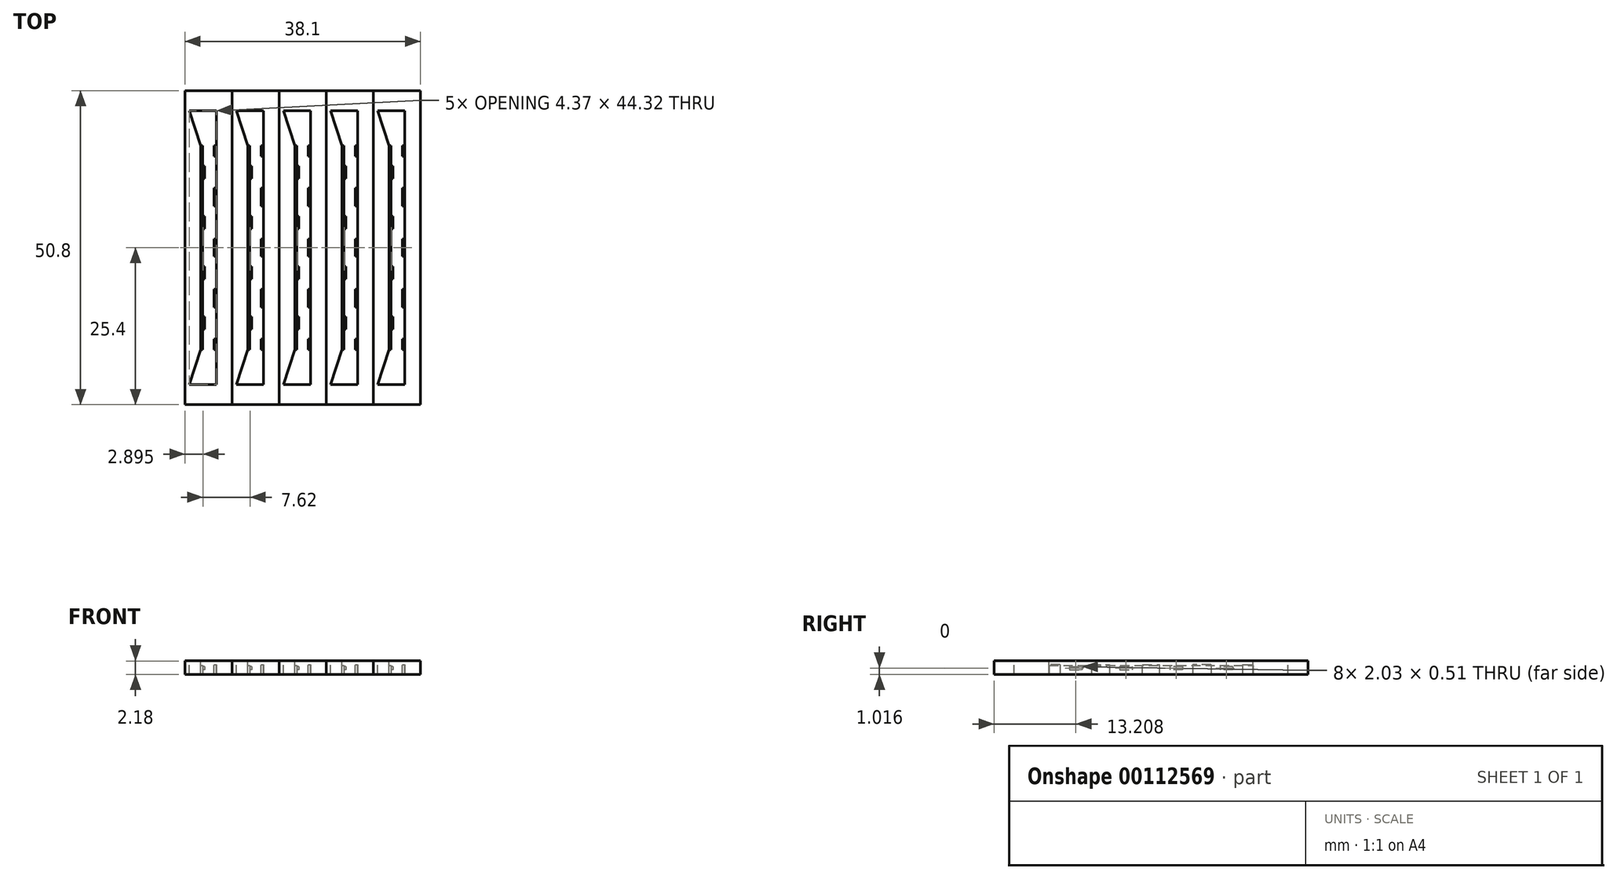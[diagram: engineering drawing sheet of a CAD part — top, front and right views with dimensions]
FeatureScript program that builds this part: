
annotation { "Feature Type Name" : "Feature", "Feature Type Description" : "" }
export const myFeature = defineFeature(function(context is Context, id is Id, definition is map)
    precondition{}
    {
        {
            var Q0;
            Q0=qCreatedBy(makeId("Top.planeOp"),FACE);
            var sketch = newSketch(context, id + "F0", { "sketchPlane" : qUnion([Q0])});
            skLineSegment(sketch, "E0.bottom", {"start": v(3.81, -25.4) * mm, "end": v(-3.81, -25.4) * mm});
            skLineSegment(sketch, "E0.top", {"start": v(3.81, 25.4) * mm, "end": v(-3.81, 25.4) * mm});
            skLineSegment(sketch, "E0.left", {"start": v(3.8, -25.4) * mm, "end": v(3.81, 25.4) * mm});
            skLineSegment(sketch, "E0.right", {"start": v(-3.81, -25.4) * mm, "end": v(-3.81, 25.4) * mm});
            skPoint(sketch, "E0.middle", {"position": v(0, 0) * mm});
            skSolve(sketch);
        }
        {
            var Q0;
            Q0=makeQuery(id+"F0.imprint","IMPRINT",FACE,{"disambiguationData":[TD([[makeQuery(id+"F0.imprint","IMPRINT",EDGE,{"derivedFrom":sQuery(id+"F0.wireOp",EDGE,"E0.bottom")}),-1.0]])]});
            extrude(context, id + "F1", {"entities" : qUnion([Q0]), "depth" : 2.18 * mm});
        }
        {
            var Q0;
            Q0=qCreatedBy(makeId("Front.planeOp"),FACE);
            var sketch = newSketch(context, id + "F2", { "sketchPlane" : qUnion([Q0])});
            skLineSegment(sketch, "E1.bottom", {"start": v(1.27, 0) * mm, "end": v(-0.97, 0) * mm});
            skLineSegment(sketch, "E1.top", {"start": v(1.27, 2.18) * mm, "end": v(-1.27, 2.18) * mm});
            skLineSegment(sketch, "E1.left", {"start": v(1.27, 0) * mm, "end": v(1.27, 2.18) * mm});
            skLineSegment(sketch, "E1.right", {"start": v(-1.27, 1.47) * mm, "end": v(-1.27, 2.18) * mm});
            skPoint(sketch, "E1.middle", {"position": v(0, 1.1) * mm});
            skLineSegment(sketch, "E2", {"start": v(-1.27, 1.47) * mm, "end": v(-0.97, 1.47) * mm});
            skLineSegment(sketch, "E3", {"start": v(-0.97, 1.47) * mm, "end": v(-0.97, 0) * mm});
            skPoint(sketch, "E4.orphan", {"position": v(-1.27, 0) * mm});
            skSolve(sketch);
        }
        {
            var Q0;
            Q0=qSketchRegion(id+"F2",true);
            extrude(context, id + "F3", {"entities" : qUnion([Q0]), "operationType" : NewBodyOperationType.REMOVE, "endBound" : BoundingType.SYMMETRIC, "depth" : 33.02 * mm});
        }
        {
            var Q0;
            Q0=makeQuery(id+"F3.boolean.opBoolean","COPY",FACE,{"derivedFrom":makeQuery(id+"F3.opExtrude","SWEPT_FACE",FACE,{"disambiguationData":[OSD([sQuery(id+"F2.wireOp",EDGE,"E1.left")])]})});
            var sketch = newSketch(context, id + "F4", { "sketchPlane" : qUnion([Q0])});
            skLineSegment(sketch, "E5.bottom", {"start": v(1.4, 0) * mm, "end": v(-1.4, 0) * mm});
            skLineSegment(sketch, "E5.top", {"start": v(1.4, 1.57) * mm, "end": v(-1.4, 1.57) * mm});
            skLineSegment(sketch, "E5.left", {"start": v(1.4, 0) * mm, "end": v(1.4, 1.57) * mm});
            skLineSegment(sketch, "E5.right", {"start": v(-1.4, 0) * mm, "end": v(-1.4, 1.57) * mm});
            skPoint(sketch, "E5.middle", {"position": v(0, 0.79) * mm});
            skLineSegment(sketch, "E6", {"start": v(0, 5.78) * mm, "end": v(0, -5.42) * mm, "construction": true});
            skLineSegment(sketch, "E7", {"start": v(-25.4, 1.57) * mm, "end": v(25.4, 1.57) * mm, "construction": true});
            skLineSegment(sketch, "E8.bottom", {"start": v(-9.68, 1.57) * mm, "end": v(-6.73, 1.57) * mm});
            skLineSegment(sketch, "E8.top", {"start": v(-9.68, 0) * mm, "end": v(-6.73, 0) * mm});
            skLineSegment(sketch, "E8.left", {"start": v(-9.68, 1.57) * mm, "end": v(-9.68, 0) * mm});
            skLineSegment(sketch, "E8.right", {"start": v(-6.73, 1.57) * mm, "end": v(-6.73, 0) * mm});
            skLineSegment(sketch, "E9.MirrorCS", {"start": v(9.68, 1.57) * mm, "end": v(9.68, 0) * mm});
            skLineSegment(sketch, "E10.MirrorCS", {"start": v(25.4, 1.57) * mm, "end": v(-25.4, 1.57) * mm, "construction": true});
            skLineSegment(sketch, "E11.MirrorCS", {"start": v(6.73, 1.57) * mm, "end": v(6.73, 0) * mm});
            skLineSegment(sketch, "E12.MirrorCS", {"start": v(9.68, 0) * mm, "end": v(6.73, 0) * mm});
            skLineSegment(sketch, "E13.MirrorCS", {"start": v(9.68, 1.57) * mm, "end": v(6.73, 1.57) * mm});
            skLineSegment(sketch, "E14.bottom", {"start": v(-14.78, 1.57) * mm, "end": v(-16.51, 1.57) * mm});
            skLineSegment(sketch, "E14.top", {"start": v(-14.78, 0) * mm, "end": v(-16.51, 0) * mm});
            skLineSegment(sketch, "E14.left", {"start": v(-14.78, 1.57) * mm, "end": v(-14.78, 0) * mm});
            skLineSegment(sketch, "E14.right", {"start": v(-16.51, 1.57) * mm, "end": v(-16.51, 0) * mm});
            skLineSegment(sketch, "E15.MirrorCS", {"start": v(14.78, 1.57) * mm, "end": v(16.51, 1.57) * mm});
            skLineSegment(sketch, "E16.MirrorCS", {"start": v(14.78, 1.57) * mm, "end": v(14.78, 0) * mm});
            skLineSegment(sketch, "E17.MirrorCS", {"start": v(14.78, 0) * mm, "end": v(16.51, 0) * mm});
            skLineSegment(sketch, "E18.MirrorCS", {"start": v(16.51, 1.57) * mm, "end": v(16.51, 0) * mm});
            skSolve(sketch);
        }
        {
            var Q0;
            Q0=qSketchRegion(id+"F4",true);
            extrude(context, id + "F5", {"entities" : qUnion([Q0]), "operationType" : NewBodyOperationType.ADD, "depth" : 0.37 * mm});
        }
        {
            var Q0;
            Q0=makeQuery(id+"F3.boolean.opBoolean","COPY",FACE,{"derivedFrom":makeQuery(id+"F3.opExtrude","SWEPT_FACE",FACE,{"disambiguationData":[OSD([sQuery(id+"F2.wireOp",EDGE,"E3")])]})});
            var sketch = newSketch(context, id + "F6", { "sketchPlane" : qUnion([Q0])});
            skLineSegment(sketch, "E19", {"start": v(0, 2.28) * mm, "end": v(0, 0) * mm, "construction": true});
            skLineSegment(sketch, "E20", {"start": v(-25.4, 1.27) * mm, "end": v(25.4, 1.27) * mm, "construction": true});
            skLineSegment(sketch, "E21", {"start": v(-25.4, 0.76) * mm, "end": v(25.4, 0.76) * mm, "construction": true});
            skLineSegment(sketch, "E22.bottom", {"start": v(-5.08, 1.27) * mm, "end": v(-3.05, 1.27) * mm});
            skLineSegment(sketch, "E22.top", {"start": v(-5.08, 0.76) * mm, "end": v(-3.05, 0.76) * mm});
            skLineSegment(sketch, "E22.left", {"start": v(-5.08, 1.27) * mm, "end": v(-5.08, 0.76) * mm});
            skLineSegment(sketch, "E22.right", {"start": v(-3.05, 1.27) * mm, "end": v(-3.05, 0.76) * mm});
            skLineSegment(sketch, "E23.MirrorCS", {"start": v(3.05, 1.27) * mm, "end": v(3.05, 0.76) * mm});
            skLineSegment(sketch, "E24.MirrorCS", {"start": v(5.08, 1.27) * mm, "end": v(5.08, 0.76) * mm});
            skLineSegment(sketch, "E25.MirrorCS", {"start": v(5.08, 0.76) * mm, "end": v(3.05, 0.76) * mm});
            skLineSegment(sketch, "E26.MirrorCS", {"start": v(5.08, 1.27) * mm, "end": v(3.05, 1.27) * mm});
            skLineSegment(sketch, "E27.bottom", {"start": v(-13.2, 1.27) * mm, "end": v(-11.18, 1.27) * mm});
            skLineSegment(sketch, "E27.top", {"start": v(-13.2, 0.76) * mm, "end": v(-11.18, 0.76) * mm});
            skLineSegment(sketch, "E27.left", {"start": v(-13.2, 1.27) * mm, "end": v(-13.2, 0.76) * mm});
            skLineSegment(sketch, "E27.right", {"start": v(-11.18, 1.27) * mm, "end": v(-11.18, 0.76) * mm});
            skLineSegment(sketch, "E28.MirrorCS", {"start": v(11.18, 1.27) * mm, "end": v(11.18, 0.76) * mm});
            skLineSegment(sketch, "E29.MirrorCS", {"start": v(13.2, 1.27) * mm, "end": v(13.2, 0.76) * mm});
            skLineSegment(sketch, "E30.MirrorCS", {"start": v(13.2, 1.27) * mm, "end": v(11.18, 1.27) * mm});
            skLineSegment(sketch, "E31.MirrorCS", {"start": v(13.2, 0.76) * mm, "end": v(11.18, 0.76) * mm});
            skSolve(sketch);
        }
        {
            var Q0;
            Q0=qSketchRegion(id+"F6",true);
            extrude(context, id + "F7", {"entities" : qUnion([Q0]), "operationType" : NewBodyOperationType.ADD, "depth" : 0.33 * mm});
        }
        {
            var Q0;
            Q0=makeQuery(id+"F1.opExtrude","CAP_FACE",FACE,{"disambiguationData":[OSD([sQuery(id+"F0.wireOp",EDGE,"E0.bottom"),sQuery(id+"F0.wireOp",EDGE,"E0.top"),sQuery(id+"F0.wireOp",EDGE,"E0.left"),sQuery(id+"F0.wireOp",EDGE,"E0.right")])],"isStart":false});
            var sketch = newSketch(context, id + "F8", { "sketchPlane" : qUnion([Q0])});
            skLineSegment(sketch, "E32", {"start": v(6, 0) * mm, "end": v(-8.25, 0) * mm, "construction": true});
            skPoint(sketch, "E32.endSnap0", {"position": v(3.81, 0) * mm});
            skLineSegment(sketch, "E33", {"start": v(-1.27, 16.51) * mm, "end": v(-3.1, 22.16) * mm});
            skLineSegment(sketch, "E34", {"start": v(-3.1, 22.16) * mm, "end": v(1.27, 22.16) * mm});
            skLineSegment(sketch, "E35", {"start": v(1.27, 22.16) * mm, "end": v(1.27, 16.51) * mm});
            skLineSegment(sketch, "E36", {"start": v(1.27, 16.51) * mm, "end": v(-1.27, 16.51) * mm});
            skLineSegment(sketch, "E37.MirrorCS", {"start": v(-1.27, -16.51) * mm, "end": v(-3.1, -22.16) * mm});
            skLineSegment(sketch, "E38.MirrorCS", {"start": v(-3.1, -22.16) * mm, "end": v(1.27, -22.16) * mm});
            skLineSegment(sketch, "E39.MirrorCS", {"start": v(1.27, -22.16) * mm, "end": v(1.27, -16.51) * mm});
            skLineSegment(sketch, "E40.MirrorCS", {"start": v(1.27, -16.51) * mm, "end": v(-1.27, -16.51) * mm});
            skSolve(sketch);
        }
        {
            var Q0;
            Q0=qSketchRegion(id+"F8",true);
            extrude(context, id + "F9", {"entities" : qUnion([Q0]), "operationType" : NewBodyOperationType.REMOVE, "oppositeDirection" : true, "depth" : 25.4 * mm});
        }
        {
            var Q0;
            Q0=makeQuery(id+"F1.opExtrude","SWEPT_BODY",BODY,{"disambiguationData":[OSD([sQuery(id+"F0.wireOp",EDGE,"E0.bottom"),sQuery(id+"F0.wireOp",EDGE,"E0.top"),sQuery(id+"F0.wireOp",EDGE,"E0.left"),sQuery(id+"F0.wireOp",EDGE,"E0.right")])]});
            transform(context, id + "F10", {"entities" : qUnion([Q0]), "transformType" : TransformType.TRANSLATION_3D, "dx" : 7.62 * mm, "dy" : 0 * mm, "dz" : 0 * mm, "makeCopy" : true});
        }
        {
            var Q0;
            Q0=makeQuery(id+"F10.opPattern","COPY",BODY,{"derivedFrom":makeQuery(id+"F1.opExtrude","SWEPT_BODY",BODY,{"disambiguationData":[OSD([sQuery(id+"F0.wireOp",EDGE,"E0.bottom"),sQuery(id+"F0.wireOp",EDGE,"E0.top"),sQuery(id+"F0.wireOp",EDGE,"E0.left"),sQuery(id+"F0.wireOp",EDGE,"E0.right")])]}),"instanceName":"1"});
            transform(context, id + "F11", {"entities" : qUnion([Q0]), "transformType" : TransformType.TRANSLATION_3D, "dx" : 7.62 * mm, "dy" : 0 * mm, "dz" : 0 * mm, "makeCopy" : true});
        }
        {
            var Q0;
            Q0=makeQuery(id+"F11.opPattern","COPY",BODY,{"derivedFrom":makeQuery(id+"F10.opPattern","COPY",BODY,{"derivedFrom":makeQuery(id+"F1.opExtrude","SWEPT_BODY",BODY,{"disambiguationData":[OSD([sQuery(id+"F0.wireOp",EDGE,"E0.bottom"),sQuery(id+"F0.wireOp",EDGE,"E0.top"),sQuery(id+"F0.wireOp",EDGE,"E0.left"),sQuery(id+"F0.wireOp",EDGE,"E0.right")])]}),"instanceName":"1"}),"instanceName":"1"});
            transform(context, id + "F12", {"entities" : qUnion([Q0]), "transformType" : TransformType.TRANSLATION_3D, "dx" : 7.62 * mm, "dy" : 0 * mm, "dz" : 0 * mm, "makeCopy" : true});
        }
        {
            var Q0;
            Q0=makeQuery(id+"F1.opExtrude","SWEPT_BODY",BODY,{"disambiguationData":[OSD([sQuery(id+"F0.wireOp",EDGE,"E0.bottom"),sQuery(id+"F0.wireOp",EDGE,"E0.top"),sQuery(id+"F0.wireOp",EDGE,"E0.left"),sQuery(id+"F0.wireOp",EDGE,"E0.right")])]});
            transform(context, id + "F13", {"entities" : qUnion([Q0]), "transformType" : TransformType.TRANSLATION_3D, "dx" : 30.48 * mm, "dy" : 0 * mm, "dz" : 0 * mm, "makeCopy" : true});
        }
    });
